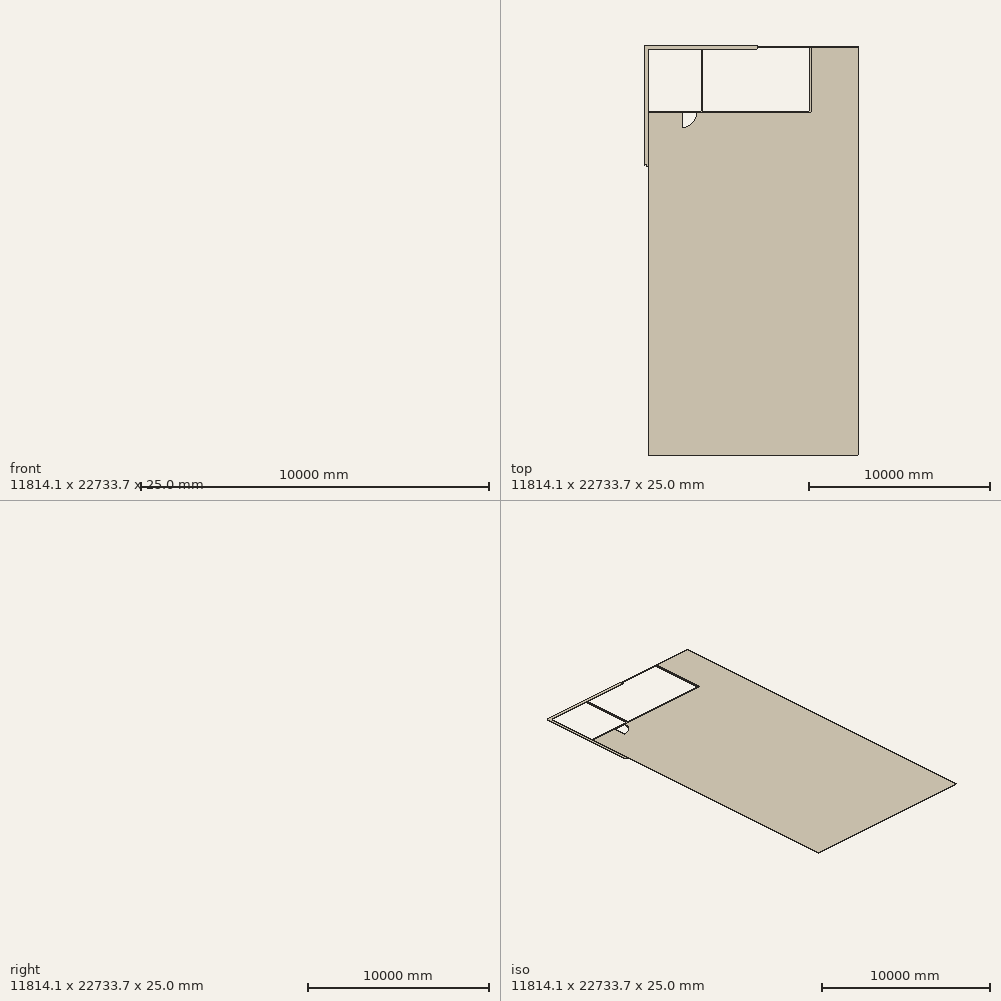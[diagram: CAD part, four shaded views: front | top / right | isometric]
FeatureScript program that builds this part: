
annotation { "Feature Type Name" : "Feature", "Feature Type Description" : "" }
export const myFeature = defineFeature(function(context is Context, id is Id, definition is map)
    precondition{}
    {
        {
            var Q0;
            Q0=qCreatedBy(makeId("Top.planeOp"),FACE);
            var sketch = newSketch(context, id + "F0", { "sketchPlane" : qUnion([Q0])});
            skLineSegment(sketch, "E0.top", {"start": v(0, -22500) * mm, "end": v(11600, -22500) * mm});
            skLineSegment(sketch, "E0.left", {"start": v(0, 0) * mm, "end": v(0, -22500) * mm});
            skLineSegment(sketch, "E0.right", {"start": v(11600, 130) * mm, "end": v(11600, -22500) * mm});
            skLineSegment(sketch, "E1.top", {"start": v(6000, 130) * mm, "end": v(11600, 130) * mm});
            skLineSegment(sketch, "E1.left", {"start": v(6000, 0) * mm, "end": v(6000, 130) * mm});
            skLineSegment(sketch, "E2", {"start": v(6000, 0) * mm, "end": v(0, 0) * mm});
            skLineSegment(sketch, "E3", {"start": v(0, -3500) * mm, "end": v(9000, -3500) * mm});
            skLineSegment(sketch, "E4", {"start": v(9000, -3500) * mm, "end": v(9000, 130) * mm});
            skLineSegment(sketch, "E5", {"start": v(8920, 130) * mm, "end": v(8920, -3420) * mm});
            skLineSegment(sketch, "E6", {"start": v(8920, -3420) * mm, "end": v(3000, -3420) * mm});
            skLineSegment(sketch, "E7", {"start": v(2920, -3420) * mm, "end": v(2920, 0) * mm});
            skLineSegment(sketch, "E8", {"start": v(3000, -3420) * mm, "end": v(3000, 0) * mm});
            skLineSegment(sketch, "E9", {"start": v(2920, -3420) * mm, "end": v(0, -3420) * mm});
            skLineSegment(sketch, "E10", {"start": v(2920, -3420) * mm, "end": v(3000, -3420) * mm, "construction": true});
            skLineSegment(sketch, "E11", {"start": v(8920, -3420) * mm, "end": v(8920, -3500) * mm, "construction": true});
            skLineSegment(sketch, "E12", {"start": v(8920, -3420) * mm, "end": v(9000, -3420) * mm, "construction": true});
            skLineSegment(sketch, "E13", {"start": v(0, -19470) * mm, "end": v(10100, -19470) * mm, "construction": true});
            skLineSegment(sketch, "E14", {"start": v(10100, -19470) * mm, "end": v(10100, -22500) * mm, "construction": true});
            skLineSegment(sketch, "E15", {"start": v(9970, -19470) * mm, "end": v(9970, -3518) * mm, "construction": true});
            skLineSegment(sketch, "E16", {"start": v(9970, -3518) * mm, "end": v(0, -3518) * mm, "construction": true});
            skLineSegment(sketch, "E17.bottom", {"start": v(12421.72, -2593.7) * mm, "end": v(13891.72, -2593.7) * mm});
            skLineSegment(sketch, "E17.top", {"start": v(12421.72, -2993.7) * mm, "end": v(13891.72, -2993.7) * mm});
            skLineSegment(sketch, "E17.left", {"start": v(12421.72, -2593.7) * mm, "end": v(12421.72, -2993.7) * mm});
            skLineSegment(sketch, "E17.right", {"start": v(13891.72, -2593.7) * mm, "end": v(13891.72, -2993.7) * mm});
            skLineSegment(sketch, "E18", {"start": v(15136.91, -3396.06) * mm, "end": v(15136.91, -5696.06) * mm});
            skLineSegment(sketch, "E19", {"start": v(15136.91, -5696.06) * mm, "end": v(15936.91, -5696.06) * mm});
            skLineSegment(sketch, "E20", {"start": v(15936.91, -5696.06) * mm, "end": v(15936.91, -4196.06) * mm});
            skLineSegment(sketch, "E21", {"start": v(15936.91, -4196.06) * mm, "end": v(16536.91, -4196.06) * mm});
            skLineSegment(sketch, "E22", {"start": v(16536.91, -4196.06) * mm, "end": v(16536.91, -3396.06) * mm});
            skLineSegment(sketch, "E23", {"start": v(16536.91, -3396.06) * mm, "end": v(15136.91, -3396.06) * mm});
            skLineSegment(sketch, "E24.bottom", {"start": v(13595.99, 0) * mm, "end": v(13995.99, 0) * mm});
            skLineSegment(sketch, "E24.top", {"start": v(13595.99, -1470) * mm, "end": v(13995.99, -1470) * mm});
            skLineSegment(sketch, "E24.left", {"start": v(13595.99, 0) * mm, "end": v(13595.99, -1470) * mm});
            skLineSegment(sketch, "E24.right", {"start": v(13995.99, 0) * mm, "end": v(13995.99, -1470) * mm});
            skLineSegment(sketch, "E25", {"start": v(16360.2, 601.2) * mm, "end": v(16360.2, -898.8) * mm});
            skLineSegment(sketch, "E26", {"start": v(16360.2, -898.8) * mm, "end": v(15760.2, -898.8) * mm});
            skLineSegment(sketch, "E27", {"start": v(15760.2, -898.8) * mm, "end": v(15760.2, -1698.8) * mm});
            skLineSegment(sketch, "E28", {"start": v(15760.2, -1698.8) * mm, "end": v(17160.2, -1698.8) * mm});
            skLineSegment(sketch, "E29", {"start": v(17160.2, -1698.8) * mm, "end": v(17160.2, 601.2) * mm});
            skLineSegment(sketch, "E30", {"start": v(17160.2, 601.2) * mm, "end": v(16360.2, 601.2) * mm});
            skArc(sketch, "E31", {"start": v(9000, -858.39) * mm, "mid": v(9579.83, -618.22) * mm, "end": v(9820, -38.39) * mm});
            skArc(sketch, "E32", {"start": v(3293.58, -3500) * mm, "mid": v(3533.75, -4079.83) * mm, "end": v(4113.58, -4320) * mm});
            skArc(sketch, "E33", {"start": v(2664.16, -3500) * mm, "mid": v(2424, -4079.83) * mm, "end": v(1844.16, -4320) * mm});
            skLineSegment(sketch, "E34", {"start": v(1844.16, -3500) * mm, "end": v(1844.16, -4320) * mm});
            skLineSegment(sketch, "E35", {"start": v(4113.58, -4320) * mm, "end": v(4113.58, -3500) * mm});
            skLineSegment(sketch, "E36", {"start": v(9000, -38.39) * mm, "end": v(9820, -38.39) * mm});
            skLineSegment(sketch, "E37", {"start": v(0, -22500) * mm, "end": v(-213.31, -22500) * mm});
            skLineSegment(sketch, "E38", {"start": v(-213.31, -22500) * mm, "end": v(-213.31, 233.66) * mm});
            skLineSegment(sketch, "E39", {"start": v(-213.31, 233.66) * mm, "end": v(6000, 233.66) * mm});
            skLineSegment(sketch, "E40", {"start": v(6000, 233.66) * mm, "end": v(6000, 130) * mm});
            skLineSegment(sketch, "E41", {"start": v(6000, 164.14) * mm, "end": v(11600.81, 164.14) * mm});
            skLineSegment(sketch, "E42", {"start": v(11600.81, 164.14) * mm, "end": v(11600, 130) * mm});
            skArc(sketch, "E43", {"start": v(-213.31, -6425.13) * mm, "mid": v(-159.98, -6371.8) * mm, "end": v(-106.66, -6425.13) * mm});
            skArc(sketch, "E44", {"start": v(-106.66, -6425.13) * mm, "mid": v(-53.33, -6478.46) * mm, "end": v(0, -6425.13) * mm});
            skSolve(sketch);
        }
        {
            var Q0;
            {var subQ14=sQuery(id+"F0.wireOp",EDGE,"E5");Q0=makeQuery(id+"F0.imprint","IMPRINT",FACE,{"disambiguationData":[TD([[makeQuery(id+"F0.imprint","IMPRINT",EDGE,{"derivedFrom":subQ14}),1.0]])]});}
            extrude(context, id + "F1", {"entities" : qUnion([Q0]), "depth" : 25 * mm, "offsetDistance" : 25 * mm});
        }
        {
            var Q0;
            {var subQ7=sQuery(id+"F0.wireOp",EDGE,"E1.left");Q0=makeQuery(id+"F0.imprint","IMPRINT",FACE,{"disambiguationData":[TD([[makeQuery(id+"F0.imprint","IMPRINT",EDGE,{"derivedFrom":subQ7}),1.0]])]});}
            var Q1;
            {var subQ6=sQuery(id+"F0.wireOp",EDGE,"E41");Q1=makeQuery(id+"F0.imprint","IMPRINT",FACE,{"disambiguationData":[TD([[makeQuery(id+"F0.imprint","IMPRINT",EDGE,{"derivedFrom":subQ6}),-1.0]])]});}
            extrude(context, id + "F2", {"entities" : qUnion([Q0, Q1]), "depth" : 25 * mm, "offsetDistance" : 25 * mm});
        }
        {
            var Q0;
            {var subQ0=sQuery(id+"F0.wireOp",EDGE,"E33");Q0=makeQuery(id+"F0.imprint","IMPRINT",FACE,{"disambiguationData":[TD([[makeQuery(id+"F0.imprint","IMPRINT",EDGE,{"derivedFrom":subQ0}),-1.0]])]});}
            var Q1;
            {var subQ0=sQuery(id+"F0.wireOp",EDGE,"E32");Q1=makeQuery(id+"F0.imprint","IMPRINT",FACE,{"disambiguationData":[TD([[makeQuery(id+"F0.imprint","IMPRINT",EDGE,{"derivedFrom":subQ0}),1.0]])]});}
            var Q2;
            {var subQ0=sQuery(id+"F0.wireOp",EDGE,"E31");Q2=makeQuery(id+"F0.imprint","IMPRINT",FACE,{"disambiguationData":[TD([[makeQuery(id+"F0.imprint","IMPRINT",EDGE,{"derivedFrom":subQ0}),1.0]])]});}
            extrude(context, id + "F3", {"entities" : qUnion([Q0, Q1, Q2]), "depth" : 25 * mm, "offsetDistance" : 25 * mm});
        }
    });
